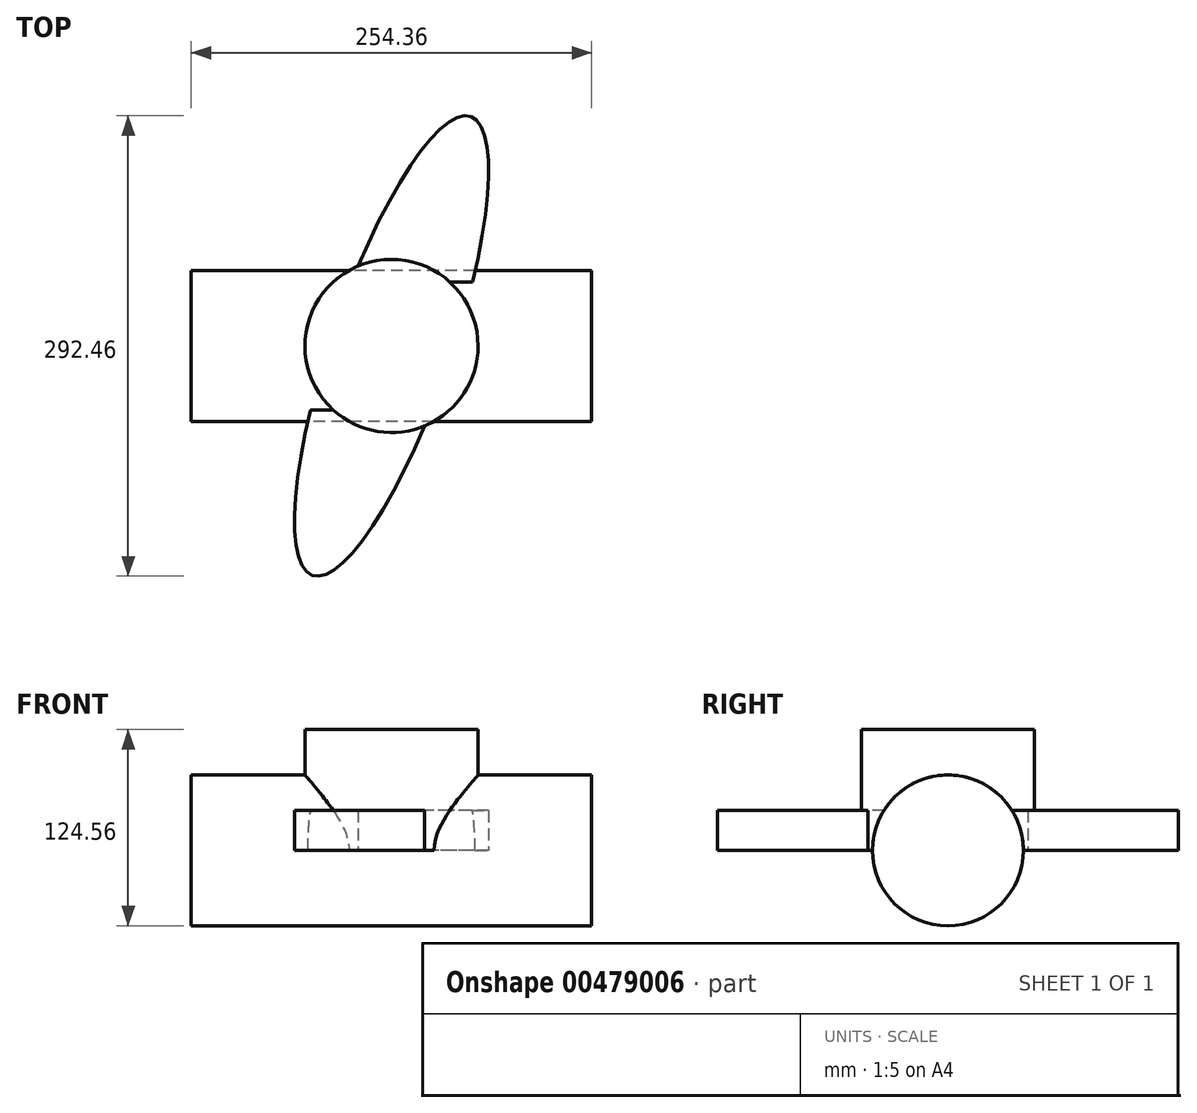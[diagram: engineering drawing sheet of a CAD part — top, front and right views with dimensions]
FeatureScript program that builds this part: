
annotation { "Feature Type Name" : "Feature", "Feature Type Description" : "" }
export const myFeature = defineFeature(function(context is Context, id is Id, definition is map)
    precondition{}
    {
        {
            var Q0;
            Q0=qCreatedBy(makeId("Top.planeOp"),FACE);
            var sketch = newSketch(context, id + "F0", { "sketchPlane" : qUnion([Q0])});
            skCircle(sketch, "E0", {"center": v(0, 0) * mm, "radius": 54.96 * mm});
            skSolve(sketch);
        }
        {
            var Q0;
            Q0 = qSketchRegion(id + "F0", true);
            extrude(context, id + "F1", {"entities" : qUnion([Q0]), "depth" : 76.68 * mm});
        }
        {
            var Q0;
            Q0=qCreatedBy(makeId("Top.planeOp"),FACE);
            var sketch = newSketch(context, id + "F2", { "sketchPlane" : qUnion([Q0])});
            skEllipse(sketch, "E1", {"center": v(0, 0) * mm, "majorRadius": 154.13 * mm, "minorRadius": 37.86 * mm, "majorAxis": v(0.33, 0.95)});
            skSolve(sketch);
        }
        {
            var Q0;
            Q0 = qSketchRegion(id + "F2", true);
            extrude(context, id + "F3", {"entities" : qUnion([Q0]), "operationType" : NewBodyOperationType.ADD, "depth" : 25.4 * mm});
        }
        {
            var Q0;
            Q0=qCreatedBy(makeId("Right.planeOp"),FACE);
            var sketch = newSketch(context, id + "F4", { "sketchPlane" : qUnion([Q0])});
            skCircle(sketch, "E2", {"center": v(0, 0) * mm, "radius": 47.88 * mm});
            skSolve(sketch);
        }
        {
            var Q0;
            Q0 = qSketchRegion(id + "F4", true);
            extrude(context, id + "F5", {"entities" : qUnion([Q0]), "operationType" : NewBodyOperationType.ADD, "endBound" : BoundingType.SYMMETRIC, "depth" : 254.36 * mm});
        }
    });
